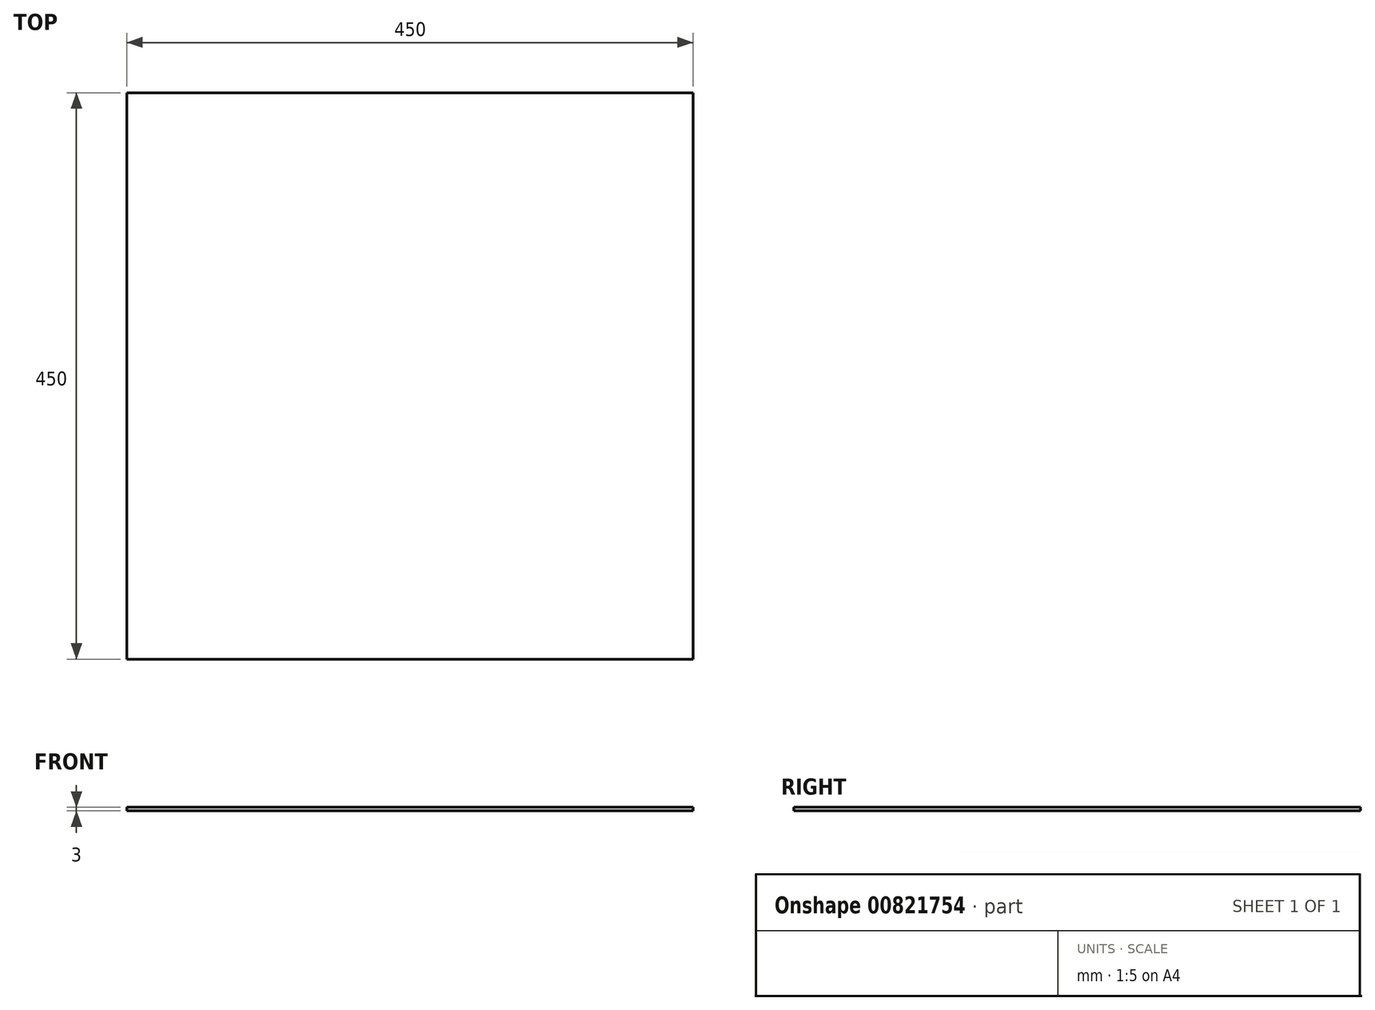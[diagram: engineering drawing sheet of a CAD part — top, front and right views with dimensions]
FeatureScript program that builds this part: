
annotation { "Feature Type Name" : "Feature", "Feature Type Description" : "" }
export const myFeature = defineFeature(function(context is Context, id is Id, definition is map)
    precondition{}
    {
        {
            var Q0;
            Q0=qCreatedBy(makeId("Top.planeOp"),FACE);
            var sketch = newSketch(context, id + "F0", { "sketchPlane" : qUnion([Q0])});
            skLineSegment(sketch, "E0.bottom", {"start": v(225, 225) * mm, "end": v(-225, 225) * mm});
            skLineSegment(sketch, "E0.top", {"start": v(225, -225) * mm, "end": v(-225, -225) * mm});
            skLineSegment(sketch, "E0.left", {"start": v(225, 225) * mm, "end": v(225, -225) * mm});
            skLineSegment(sketch, "E0.right", {"start": v(-225, 225) * mm, "end": v(-225, -225) * mm});
            skPoint(sketch, "E0.middle", {"position": v(0, 0) * mm});
            skSolve(sketch);
        }
        {
            var Q0;
            Q0 = qSketchRegion(id + "F0", true);
            extrude(context, id + "F1", {"entities" : qUnion([Q0]), "depth" : 3 * mm, "offsetDistance" : 25 * mm});
        }
    });
